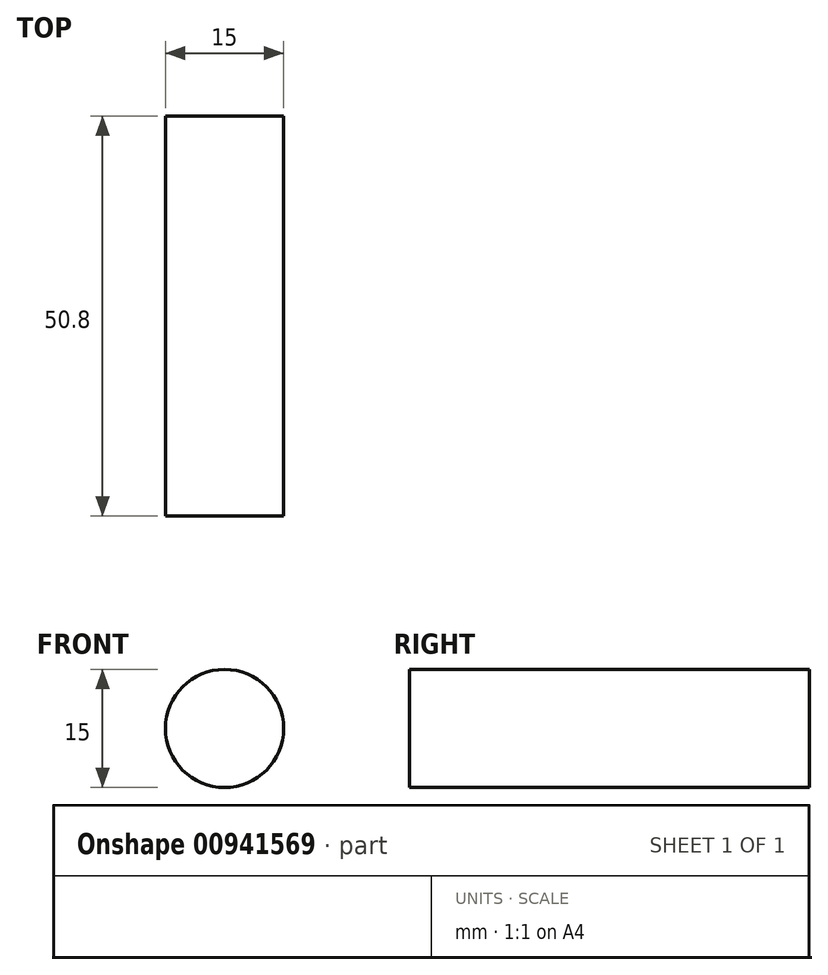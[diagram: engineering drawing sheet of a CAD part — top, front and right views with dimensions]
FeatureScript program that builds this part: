
annotation { "Feature Type Name" : "Feature", "Feature Type Description" : "" }
export const myFeature = defineFeature(function(context is Context, id is Id, definition is map)
    precondition{}
    {
        {
            var Q0;
            Q0=qCreatedBy(makeId("Front.planeOp"),FACE);
            var sketch = newSketch(context, id + "F0", { "sketchPlane" : qUnion([Q0])});
            skCircle(sketch, "E0", {"center": v(0, 0) * mm, "radius": 7.5 * mm});
            skSolve(sketch);
        }
        {
            var Q0;
            Q0=makeQuery(id+"F0.imprint","IMPRINT",FACE,{"disambiguationData":[TD([[makeQuery(id+"F0.imprint","IMPRINT",EDGE,{"derivedFrom":sQuery(id+"F0.wireOp",EDGE,"E0")}),1.0]])]});
            extrude(context, id + "F1", {"entities" : qUnion([Q0]), "endBound" : BoundingType.SYMMETRIC, "depth" : 50.8 * mm, "offsetDistance" : 25.4 * mm});
        }
    });
